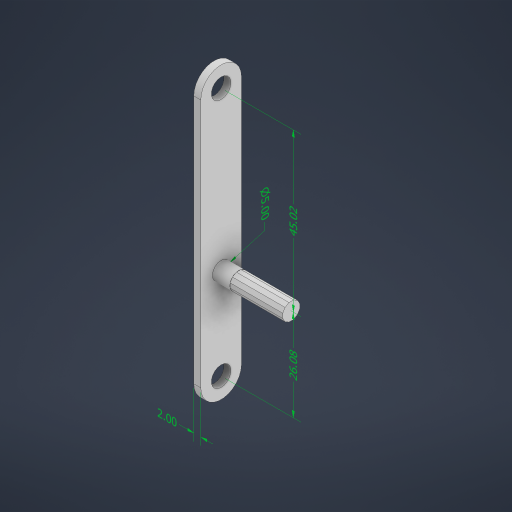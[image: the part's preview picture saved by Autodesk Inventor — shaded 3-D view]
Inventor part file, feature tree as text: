
AUTODESK INVENTOR PART (.ipt)
format: ipt  version: 2024 (Build 280153000, 153)  size: 393,216 bytes
history: native  units: mm
features: other x5, extrude x3, sketch x1
ambient origin geometry x8: Origin, YZ Plane, XZ Plane, XY Plane, X Axis, Y Axis, Z Axis, Center Point
bodies: Body1 (feature_tree)
feature tree (9):
  other  "솔리드1"
  sketch  "스케치1"
  extrude  "돌출1"  Depth=5.6mm
  extrude  "돌출2"  Depth=5.6mm
  extrude  "돌출3"  Depth=11.6mm
  other  "선형 치수 1"
  other  "선형 치수 2"
  other  "선형 치수 3"
  other  "지름 치수 1"
